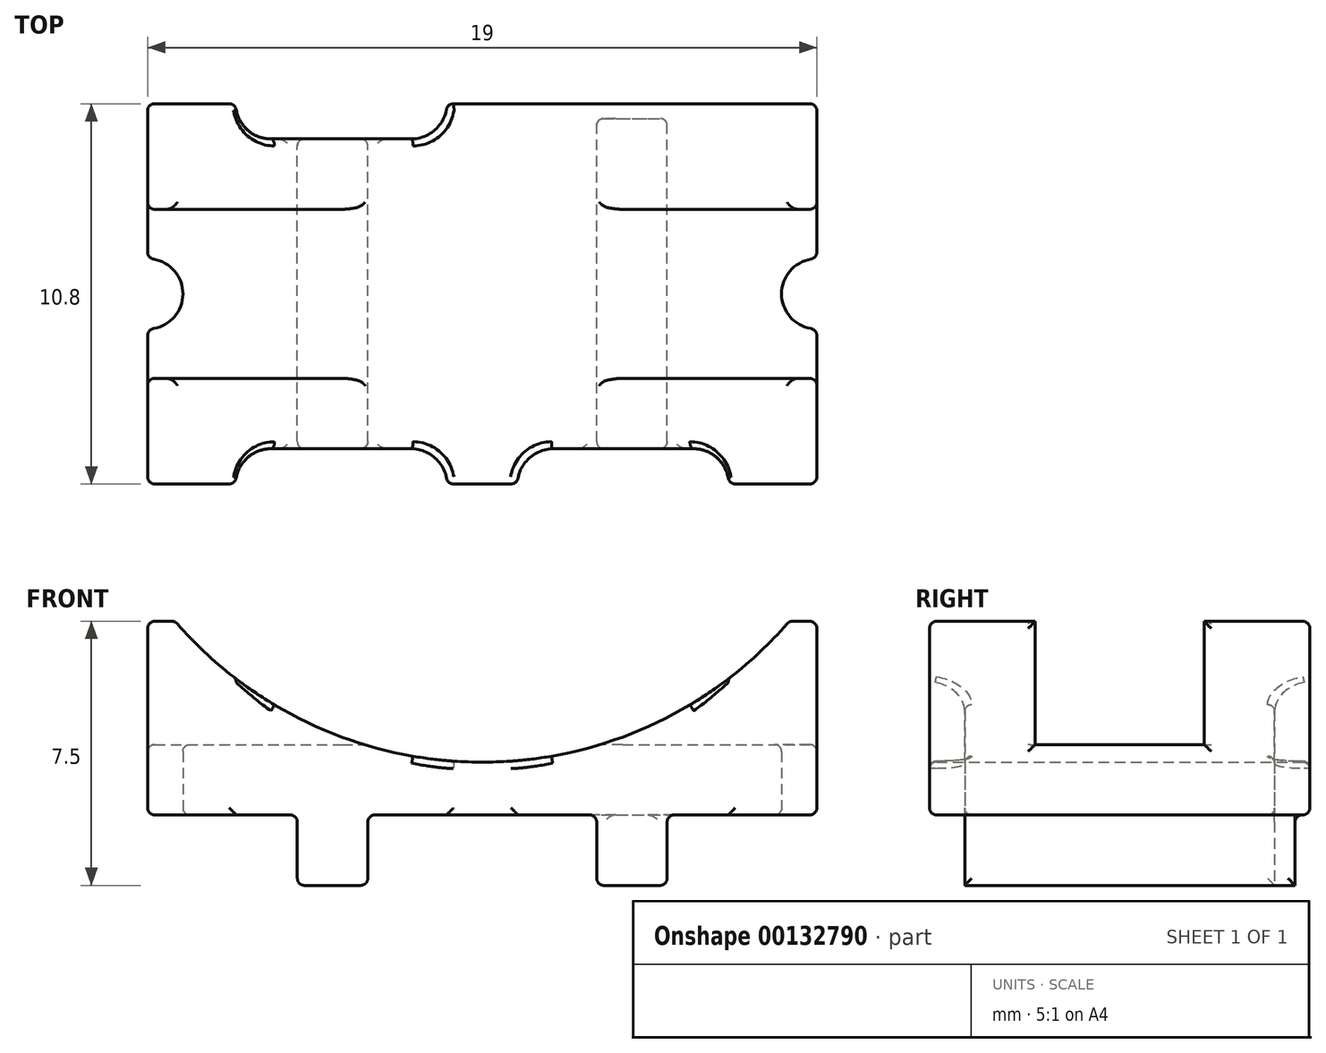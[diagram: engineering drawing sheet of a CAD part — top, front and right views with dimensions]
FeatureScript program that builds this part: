
annotation { "Feature Type Name" : "Feature", "Feature Type Description" : "" }
export const myFeature = defineFeature(function(context is Context, id is Id, definition is map)
    precondition{}
    {
        {
            var Q0;
            Q0=qCreatedBy(makeId("Top.planeOp"),FACE);
            var sketch = newSketch(context, id + "F0", { "sketchPlane" : qUnion([Q0])});
            skLineSegment(sketch, "E0.bottom", {"start": v(-9.5, -5.4) * mm, "end": v(9.5, -5.4) * mm});
            skLineSegment(sketch, "E0.top", {"start": v(-9.5, 5.4) * mm, "end": v(9.5, 5.4) * mm});
            skLineSegment(sketch, "E0.left", {"start": v(-9.5, -5.4) * mm, "end": v(-9.5, 5.4) * mm});
            skLineSegment(sketch, "E0.right", {"start": v(9.5, -5.4) * mm, "end": v(9.5, 5.4) * mm});
            skSolve(sketch);
        }
        {
            var Q0;
            Q0=makeQuery(id+"F0.imprint","IMPRINT",FACE,{"disambiguationData":[TD([[makeQuery(id+"F0.imprint","IMPRINT",EDGE,{"derivedFrom":sQuery(id+"F0.wireOp",EDGE,"E0.bottom")}),1.0]])]});
            extrude(context, id + "F1", {"entities" : qUnion([Q0]), "depth" : 7.5 * mm, "hasSecondDirection" : true, "secondDirectionOppositeDirection" : false, "secondDirectionDepth" : 2 * mm});
        }
        {
            var Q0;
            Q0=qCreatedBy(makeId("Top.planeOp"),FACE);
            var sketch = newSketch(context, id + "F2", { "sketchPlane" : qUnion([Q0])});
            skLineSegment(sketch, "E1.bottom", {"start": v(-5.25, -5.02) * mm, "end": v(-3.25, -5.02) * mm});
            skLineSegment(sketch, "E1.top", {"start": v(-5.25, 4.98) * mm, "end": v(-3.25, 4.98) * mm});
            skLineSegment(sketch, "E1.left", {"start": v(-5.25, -5.02) * mm, "end": v(-5.25, 4.98) * mm});
            skLineSegment(sketch, "E1.right", {"start": v(-3.25, -5.02) * mm, "end": v(-3.25, 4.98) * mm});
            skLineSegment(sketch, "E2.bottom", {"start": v(3.25, -5.02) * mm, "end": v(5.25, -5.02) * mm});
            skLineSegment(sketch, "E2.top", {"start": v(3.25, 4.98) * mm, "end": v(5.25, 4.98) * mm});
            skLineSegment(sketch, "E2.left", {"start": v(3.25, -5.02) * mm, "end": v(3.25, 4.98) * mm});
            skLineSegment(sketch, "E2.right", {"start": v(5.25, -5.02) * mm, "end": v(5.25, 4.98) * mm});
            skSolve(sketch);
        }
        {
            var Q0;
            Q0=makeQuery(id+"F2.imprint","IMPRINT",FACE,{"disambiguationData":[TD([[makeQuery(id+"F2.imprint","IMPRINT",EDGE,{"derivedFrom":sQuery(id+"F2.wireOp",EDGE,"E2.bottom")}),1.0]])]});
            var Q1;
            Q1=makeQuery(id+"F2.imprint","IMPRINT",FACE,{"disambiguationData":[TD([[makeQuery(id+"F2.imprint","IMPRINT",EDGE,{"derivedFrom":sQuery(id+"F2.wireOp",EDGE,"E1.bottom")}),1.0]])]});
            extrude(context, id + "F3", {"entities" : qUnion([Q0, Q1]), "operationType" : NewBodyOperationType.ADD, "depth" : 2 * mm});
        }
        {
            var Q0;
            Q0=qCreatedBy(makeId("Top.planeOp"),FACE);
            var sketch = newSketch(context, id + "F4", { "sketchPlane" : qUnion([Q0])});
            skLineSegment(sketch, "E3.bottom", {"start": v(-13, 2.4) * mm, "end": v(13, 2.4) * mm});
            skLineSegment(sketch, "E3.top", {"start": v(-13, -2.4) * mm, "end": v(13, -2.4) * mm});
            skLineSegment(sketch, "E3.left", {"start": v(-13, 2.4) * mm, "end": v(-13, -2.4) * mm});
            skLineSegment(sketch, "E3.right", {"start": v(13, 2.4) * mm, "end": v(13, -2.4) * mm});
            skSolve(sketch);
        }
        {
            var Q0;
            Q0=makeQuery(id+"F4.imprint","IMPRINT",FACE,{"disambiguationData":[TD([[makeQuery(id+"F4.imprint","IMPRINT",EDGE,{"derivedFrom":sQuery(id+"F4.wireOp",EDGE,"E3.bottom")}),-1.0]])]});
            extrude(context, id + "F5", {"entities" : qUnion([Q0]), "operationType" : NewBodyOperationType.REMOVE, "depth" : 10 * mm, "hasSecondDirection" : true, "secondDirectionOppositeDirection" : false, "secondDirectionDepth" : 4 * mm});
        }
        {
            var Q0;
            Q0=qCreatedBy(makeId("Front.planeOp"),FACE);
            var sketch = newSketch(context, id + "F6", { "sketchPlane" : qUnion([Q0])});
            skCircle(sketch, "E4", {"center": v(0, 15) * mm, "radius": 11.5 * mm});
            skSolve(sketch);
        }
        {
            var Q0;
            Q0=makeQuery(id+"F6.imprint","IMPRINT",FACE,{"disambiguationData":[TD([[makeQuery(id+"F6.imprint","IMPRINT",EDGE,{"derivedFrom":sQuery(id+"F6.wireOp",EDGE,"E4")}),1.0]])]});
            extrude(context, id + "F7", {"entities" : qUnion([Q0]), "operationType" : NewBodyOperationType.REMOVE, "endBound" : BoundingType.SYMMETRIC, "depth" : 25 * mm});
        }
        {
            var Q0;
            Q0=qCreatedBy(makeId("Top.planeOp"),FACE);
            var sketch = newSketch(context, id + "F8", { "sketchPlane" : qUnion([Q0])});
            skCircle(sketch, "E5", {"center": v(-9.5, 0) * mm, "radius": 1 * mm});
            skCircle(sketch, "E6", {"center": v(9.5, 0) * mm, "radius": 1 * mm});
            skLineSegment(sketch, "E7.bottom", {"start": v(-7, 6.4) * mm, "end": v(-1, 6.4) * mm});
            skLineSegment(sketch, "E7.top", {"start": v(-6, 4.4) * mm, "end": v(-2, 4.4) * mm});
            skLineSegment(sketch, "E7.left", {"start": v(-7, 6.4) * mm, "end": v(-7, 5.4) * mm});
            skLineSegment(sketch, "E7.right", {"start": v(-1, 6.4) * mm, "end": v(-1, 5.4) * mm});
            skPoint(sketch, "E8.visualSharp", {"position": v(-7, 4.4) * mm});
            skArc(sketch, "E8.filletArc", {"start": v(-7, 5.4) * mm, "mid": v(-6.7, 4.7) * mm, "end": v(-6, 4.4) * mm});
            skPoint(sketch, "E9.visualSharp", {"position": v(-1, 4.4) * mm});
            skArc(sketch, "E9.filletArc", {"start": v(-2, 4.4) * mm, "mid": v(-1.3, 4.7) * mm, "end": v(-1, 5.4) * mm});
            skArc(sketch, "E10.MirrorCS", {"start": v(2, 4.4) * mm, "mid": v(1.3, 4.7) * mm, "end": v(1, 5.4) * mm});
            skArc(sketch, "E11.MirrorCS", {"start": v(7, 5.4) * mm, "mid": v(6.7, 4.7) * mm, "end": v(6, 4.4) * mm});
            skLineSegment(sketch, "E12.MirrorCS", {"start": v(1, 6.4) * mm, "end": v(1, 5.4) * mm});
            skPoint(sketch, "E13.MirrorP", {"position": v(1, 4.4) * mm});
            skLineSegment(sketch, "E14.MirrorCS", {"start": v(7, 6.4) * mm, "end": v(7, 5.4) * mm});
            skPoint(sketch, "E15.MirrorP", {"position": v(7, 4.4) * mm});
            skLineSegment(sketch, "E16.MirrorCS", {"start": v(6, 4.4) * mm, "end": v(2, 4.4) * mm});
            skLineSegment(sketch, "E17.MirrorCS", {"start": v(7, 6.4) * mm, "end": v(1, 6.4) * mm});
            skPoint(sketch, "E18.MirrorP", {"position": v(-1, -4.4) * mm});
            skArc(sketch, "E19.MirrorCS", {"start": v(7, -5.4) * mm, "mid": v(6.7, -4.7) * mm, "end": v(6, -4.4) * mm});
            skPoint(sketch, "E20.MirrorP", {"position": v(7, -4.4) * mm});
            skArc(sketch, "E21.MirrorCS", {"start": v(-2, -4.4) * mm, "mid": v(-1.3, -4.7) * mm, "end": v(-1, -5.4) * mm});
            skLineSegment(sketch, "E22.MirrorCS", {"start": v(-1, -6.4) * mm, "end": v(-1, -5.4) * mm});
            skPoint(sketch, "E23.MirrorP", {"position": v(-7, -4.4) * mm});
            skLineSegment(sketch, "E24.MirrorCS", {"start": v(1, -6.4) * mm, "end": v(1, -5.4) * mm});
            skPoint(sketch, "E25.MirrorP", {"position": v(1, -4.4) * mm});
            skArc(sketch, "E26.MirrorCS", {"start": v(2, -4.4) * mm, "mid": v(1.3, -4.7) * mm, "end": v(1, -5.4) * mm});
            skLineSegment(sketch, "E27.MirrorCS", {"start": v(7, -6.4) * mm, "end": v(1, -6.4) * mm});
            skLineSegment(sketch, "E28.MirrorCS", {"start": v(6, -4.4) * mm, "end": v(2, -4.4) * mm});
            skLineSegment(sketch, "E29.MirrorCS", {"start": v(7, -6.4) * mm, "end": v(7, -5.4) * mm});
            skArc(sketch, "E30.MirrorCS", {"start": v(-7, -5.4) * mm, "mid": v(-6.7, -4.7) * mm, "end": v(-6, -4.4) * mm});
            skLineSegment(sketch, "E31.MirrorCS", {"start": v(-6, -4.4) * mm, "end": v(-2, -4.4) * mm});
            skLineSegment(sketch, "E32.MirrorCS", {"start": v(-7, -6.4) * mm, "end": v(-7, -5.4) * mm});
            skLineSegment(sketch, "E33.MirrorCS", {"start": v(-7, -6.4) * mm, "end": v(-1, -6.4) * mm});
            skSolve(sketch);
        }
        {
            var Q0;
            Q0=makeQuery(id+"F8.imprint","IMPRINT",FACE,{"disambiguationData":[TD([[makeQuery(id+"F8.imprint","IMPRINT",EDGE,{"derivedFrom":sQuery(id+"F8.wireOp",EDGE,"E5")}),1.0]])]});
            var Q1;
            Q1=makeQuery(id+"F8.imprint","IMPRINT",FACE,{"disambiguationData":[TD([[makeQuery(id+"F8.imprint","IMPRINT",EDGE,{"derivedFrom":sQuery(id+"F8.wireOp",EDGE,"E7.top")}),1.0]])]});
            var Q2;
            Q2=makeQuery(id+"F8.imprint","IMPRINT",FACE,{"disambiguationData":[TD([[makeQuery(id+"F8.imprint","IMPRINT",EDGE,{"derivedFrom":sQuery(id+"F8.wireOp",EDGE,"E10.MirrorCS")}),-1.0]])]});
            var Q3;
            Q3=makeQuery(id+"F8.imprint","IMPRINT",FACE,{"disambiguationData":[TD([[makeQuery(id+"F8.imprint","IMPRINT",EDGE,{"derivedFrom":sQuery(id+"F8.wireOp",EDGE,"E6")}),1.0]])]});
            var Q4;
            Q4=makeQuery(id+"F8.imprint","IMPRINT",FACE,{"disambiguationData":[TD([[makeQuery(id+"F8.imprint","IMPRINT",EDGE,{"derivedFrom":sQuery(id+"F8.wireOp",EDGE,"E27.MirrorCS")}),-1.0]])]});
            var Q5;
            Q5=makeQuery(id+"F8.imprint","IMPRINT",FACE,{"disambiguationData":[TD([[makeQuery(id+"F8.imprint","IMPRINT",EDGE,{"derivedFrom":sQuery(id+"F8.wireOp",EDGE,"E33.MirrorCS")}),1.0]])]});
            extrude(context, id + "F9", {"entities" : qUnion([Q0, Q1, Q2, Q3, Q4, Q5]), "operationType" : NewBodyOperationType.REMOVE, "depth" : 10 * mm});
        }
        {
            var Q0;
            {var subQ0=sQuery(id+"F0.wireOp",EDGE,"E0.bottom");var subQ1=sQuery(id+"F0.wireOp",EDGE,"E0.left");Q0=makeQuery(id+"F5.boolean.opBoolean","SPLIT",EDGE,{"disambiguationData":[TD([makeQuery(id+"F1.opExtrude","SWEPT_FACE",FACE,{"disambiguationData":[OSD([subQ0])]})])],"derivedFrom":makeQuery(id+"F1.opExtrude","CAP_EDGE",EDGE,{"disambiguationData":[OSD([subQ1])],"isStart":false})});}
            var Q1;
            Q1=makeQuery(id+"F7.boolean.opBoolean","COPY",FACE,{"derivedFrom":makeQuery(id+"F7.opExtrude","SWEPT_FACE",FACE,{"disambiguationData":[OSD([sQuery(id+"F6.wireOp",EDGE,"E4")])]})});
            var Q2;
            {var subQ1=sQuery(id+"F0.wireOp",EDGE,"E0.right");var subQ4=sQuery(id+"F0.wireOp",EDGE,"E0.bottom");Q2=makeQuery(id+"F9.boolean.opBoolean","SPLIT",FACE,{"disambiguationData":[TD([makeQuery(id+"F1.opExtrude","SWEPT_FACE",FACE,{"disambiguationData":[OSD([subQ4])]})])],"derivedFrom":makeQuery(id+"F1.opExtrude","SWEPT_FACE",FACE,{"disambiguationData":[OSD([subQ1])]})});}
            var Q3;
            {var subQ1=sQuery(id+"F0.wireOp",EDGE,"E0.top");var subQ2=sQuery(id+"F0.wireOp",EDGE,"E0.right");Q3=makeQuery(id+"F9.boolean.opBoolean","SPLIT",FACE,{"disambiguationData":[TD([makeQuery(id+"F1.opExtrude","SWEPT_FACE",FACE,{"disambiguationData":[OSD([subQ1])]})])],"derivedFrom":makeQuery(id+"F1.opExtrude","SWEPT_FACE",FACE,{"disambiguationData":[OSD([subQ2])]})});}
            var Q4;
            {var subQ0=sQuery(id+"F0.wireOp",EDGE,"E0.right");var subQ3=sQuery(id+"F0.wireOp",EDGE,"E0.bottom");Q4=makeQuery(id+"F9.boolean.opBoolean","SPLIT",FACE,{"disambiguationData":[TD([makeQuery(id+"F1.opExtrude","SWEPT_FACE",FACE,{"disambiguationData":[OSD([subQ0])]})])],"derivedFrom":makeQuery(id+"F1.opExtrude","SWEPT_FACE",FACE,{"disambiguationData":[OSD([subQ3])]})});}
            var Q5;
            {var subQ0=sQuery(id+"F0.wireOp",EDGE,"E0.bottom");Q5=makeQuery(id+"F9.boolean.opBoolean","SPLIT",FACE,{"disambiguationData":[TD([makeQuery(id+"F9.opExtrude","SWEPT_FACE",FACE,{"disambiguationData":[OSD([sQuery(id+"F8.wireOp",EDGE,"E26.MirrorCS")])]})])],"derivedFrom":makeQuery(id+"F1.opExtrude","SWEPT_FACE",FACE,{"disambiguationData":[OSD([subQ0])]})});}
            var Q6;
            {var subQ0=sQuery(id+"F0.wireOp",EDGE,"E0.left");var subQ3=sQuery(id+"F0.wireOp",EDGE,"E0.bottom");Q6=makeQuery(id+"F9.boolean.opBoolean","SPLIT",FACE,{"disambiguationData":[TD([makeQuery(id+"F1.opExtrude","SWEPT_FACE",FACE,{"disambiguationData":[OSD([subQ0])]})])],"derivedFrom":makeQuery(id+"F1.opExtrude","SWEPT_FACE",FACE,{"disambiguationData":[OSD([subQ3])]})});}
            var Q7;
            {var subQ2=sQuery(id+"F0.wireOp",EDGE,"E0.left");var subQ4=sQuery(id+"F0.wireOp",EDGE,"E0.bottom");Q7=makeQuery(id+"F9.boolean.opBoolean","SPLIT",FACE,{"disambiguationData":[TD([makeQuery(id+"F1.opExtrude","SWEPT_FACE",FACE,{"disambiguationData":[OSD([subQ4])]})])],"derivedFrom":makeQuery(id+"F1.opExtrude","SWEPT_FACE",FACE,{"disambiguationData":[OSD([subQ2])]})});}
            var Q8;
            {var subQ1=sQuery(id+"F0.wireOp",EDGE,"E0.top");var subQ3=sQuery(id+"F0.wireOp",EDGE,"E0.left");Q8=makeQuery(id+"F9.boolean.opBoolean","SPLIT",FACE,{"disambiguationData":[TD([makeQuery(id+"F1.opExtrude","SWEPT_FACE",FACE,{"disambiguationData":[OSD([subQ1])]})])],"derivedFrom":makeQuery(id+"F1.opExtrude","SWEPT_FACE",FACE,{"disambiguationData":[OSD([subQ3])]})});}
            var Q9;
            {var subQ0=sQuery(id+"F0.wireOp",EDGE,"E0.left");var subQ2=sQuery(id+"F0.wireOp",EDGE,"E0.top");Q9=makeQuery(id+"F9.boolean.opBoolean","SPLIT",FACE,{"disambiguationData":[TD([makeQuery(id+"F1.opExtrude","SWEPT_FACE",FACE,{"disambiguationData":[OSD([subQ0])]})])],"derivedFrom":makeQuery(id+"F1.opExtrude","SWEPT_FACE",FACE,{"disambiguationData":[OSD([subQ2])]})});}
            var Q10;
            {var subQ0=sQuery(id+"F0.wireOp",EDGE,"E0.top");Q10=makeQuery(id+"F9.boolean.opBoolean","SPLIT",FACE,{"disambiguationData":[TD([makeQuery(id+"F9.opExtrude","SWEPT_FACE",FACE,{"disambiguationData":[OSD([sQuery(id+"F8.wireOp",EDGE,"E9.filletArc")])]})])],"derivedFrom":makeQuery(id+"F1.opExtrude","SWEPT_FACE",FACE,{"disambiguationData":[OSD([subQ0])]})});}
            var Q11;
            {var subQ0=sQuery(id+"F0.wireOp",EDGE,"E0.right");var subQ2=sQuery(id+"F0.wireOp",EDGE,"E0.top");Q11=makeQuery(id+"F9.boolean.opBoolean","SPLIT",FACE,{"disambiguationData":[TD([makeQuery(id+"F1.opExtrude","SWEPT_FACE",FACE,{"disambiguationData":[OSD([subQ0])]})])],"derivedFrom":makeQuery(id+"F1.opExtrude","SWEPT_FACE",FACE,{"disambiguationData":[OSD([subQ2])]})});}
            var Q12;
            Q12=makeQuery(id+"F3.opExtrude","SWEPT_FACE",FACE,{"disambiguationData":[OSD([sQuery(id+"F2.wireOp",EDGE,"E1.right")])]});
            var Q13;
            Q13=makeQuery(id+"F3.opExtrude","SWEPT_FACE",FACE,{"disambiguationData":[OSD([sQuery(id+"F2.wireOp",EDGE,"E2.right")])]});
            var Q14;
            Q14=makeQuery(id+"F3.opExtrude","SWEPT_FACE",FACE,{"disambiguationData":[OSD([sQuery(id+"F2.wireOp",EDGE,"E2.left")])]});
            var Q15;
            Q15=makeQuery(id+"F3.opExtrude","SWEPT_FACE",FACE,{"disambiguationData":[OSD([sQuery(id+"F2.wireOp",EDGE,"E1.left")])]});
            var Q16;
            Q16=makeQuery(id+"F9.boolean.opBoolean","COPY",EDGE,{"derivedFrom":makeQuery(id+"F9.opExtrude","CAP_EDGE",EDGE,{"disambiguationData":[OSD([sQuery(id+"F8.wireOp",EDGE,"E31.MirrorCS")])],"isStart":true})});
            var Q17;
            Q17=makeQuery(id+"F9.boolean.opBoolean","COPY",EDGE,{"derivedFrom":makeQuery(id+"F9.opExtrude","CAP_EDGE",EDGE,{"disambiguationData":[OSD([sQuery(id+"F8.wireOp",EDGE,"E28.MirrorCS")])],"isStart":true})});
            var Q18;
            Q18=makeQuery(id+"F9.boolean.opBoolean","COPY",EDGE,{"derivedFrom":makeQuery(id+"F9.opExtrude","CAP_EDGE",EDGE,{"disambiguationData":[OSD([sQuery(id+"F8.wireOp",EDGE,"E7.top")])],"isStart":true})});
            var Q19;
            Q19=makeQuery(id+"F9.boolean.opBoolean","COPY",EDGE,{"derivedFrom":makeQuery(id+"F9.opExtrude","CAP_EDGE",EDGE,{"disambiguationData":[OSD([sQuery(id+"F8.wireOp",EDGE,"E16.MirrorCS")])],"isStart":true})});
            var Q20;
            Q20=makeQuery(id+"F9.boolean.opBoolean","INTERSECT",EDGE,{"derivedFrom":[makeQuery(id+"F1.opExtrude","CAP_FACE",FACE,{"disambiguationData":[OSD([sQuery(id+"F0.wireOp",EDGE,"E0.bottom"),sQuery(id+"F0.wireOp",EDGE,"E0.top"),sQuery(id+"F0.wireOp",EDGE,"E0.left"),sQuery(id+"F0.wireOp",EDGE,"E0.right")])],"isStart":true}),makeQuery(id+"F9.opExtrude","SWEPT_FACE",FACE,{"disambiguationData":[OSD([sQuery(id+"F8.wireOp",EDGE,"E6")])]})]});
            var Q21;
            Q21=makeQuery(id+"F9.boolean.opBoolean","INTERSECT",EDGE,{"derivedFrom":[makeQuery(id+"F1.opExtrude","CAP_FACE",FACE,{"disambiguationData":[OSD([sQuery(id+"F0.wireOp",EDGE,"E0.bottom"),sQuery(id+"F0.wireOp",EDGE,"E0.top"),sQuery(id+"F0.wireOp",EDGE,"E0.left"),sQuery(id+"F0.wireOp",EDGE,"E0.right")])],"isStart":true}),makeQuery(id+"F9.opExtrude","SWEPT_FACE",FACE,{"disambiguationData":[OSD([sQuery(id+"F8.wireOp",EDGE,"E5")])]})]});
            var Q22;
            {var subQ0=sQuery(id+"F4.wireOp",EDGE,"E3.bottom");var subQ1=sQuery(id+"F4.wireOp",EDGE,"E3.top");Q22=makeQuery(id+"F9.boolean.opBoolean","INTERSECT",EDGE,{"derivedFrom":[makeQuery(id+"F7.boolean.opBoolean","SPLIT",FACE,{"disambiguationData":[TD([makeQuery(id+"F1.opExtrude","SWEPT_FACE",FACE,{"disambiguationData":[OSD([sQuery(id+"F0.wireOp",EDGE,"E0.left")])]})])],"derivedFrom":makeQuery(id+"F5.boolean.opBoolean","COPY",FACE,{"derivedFrom":makeQuery(id+"F5.opExtrude","CAP_FACE",FACE,{"disambiguationData":[OSD([subQ0,subQ1,sQuery(id+"F4.wireOp",EDGE,"E3.left"),sQuery(id+"F4.wireOp",EDGE,"E3.right")])],"isStart":true})})}),makeQuery(id+"F9.opExtrude","SWEPT_FACE",FACE,{"disambiguationData":[OSD([sQuery(id+"F8.wireOp",EDGE,"E5")])]})]});}
            var Q23;
            {var subQ0=sQuery(id+"F4.wireOp",EDGE,"E3.bottom");var subQ1=sQuery(id+"F4.wireOp",EDGE,"E3.top");Q23=makeQuery(id+"F9.boolean.opBoolean","INTERSECT",EDGE,{"derivedFrom":[makeQuery(id+"F7.boolean.opBoolean","SPLIT",FACE,{"disambiguationData":[TD([makeQuery(id+"F1.opExtrude","SWEPT_FACE",FACE,{"disambiguationData":[OSD([sQuery(id+"F0.wireOp",EDGE,"E0.right")])]})])],"derivedFrom":makeQuery(id+"F5.boolean.opBoolean","COPY",FACE,{"derivedFrom":makeQuery(id+"F5.opExtrude","CAP_FACE",FACE,{"disambiguationData":[OSD([subQ0,subQ1,sQuery(id+"F4.wireOp",EDGE,"E3.left"),sQuery(id+"F4.wireOp",EDGE,"E3.right")])],"isStart":true})})}),makeQuery(id+"F9.opExtrude","SWEPT_FACE",FACE,{"disambiguationData":[OSD([sQuery(id+"F8.wireOp",EDGE,"E6")])]})]});}
            fillet(context, id + "F10", {"entities" : qUnion([Q0, Q1, Q2, Q3, Q4, Q5, Q6, Q7, Q8, Q9, Q10, Q11, Q12, Q13, Q14, Q15, Q16, Q17, Q18, Q19, Q20, Q21, Q22, Q23]), "radius" : 0.2 * mm, "tangentPropagation" : true, "allowEdgeOverflow" : false});
        }
    });
